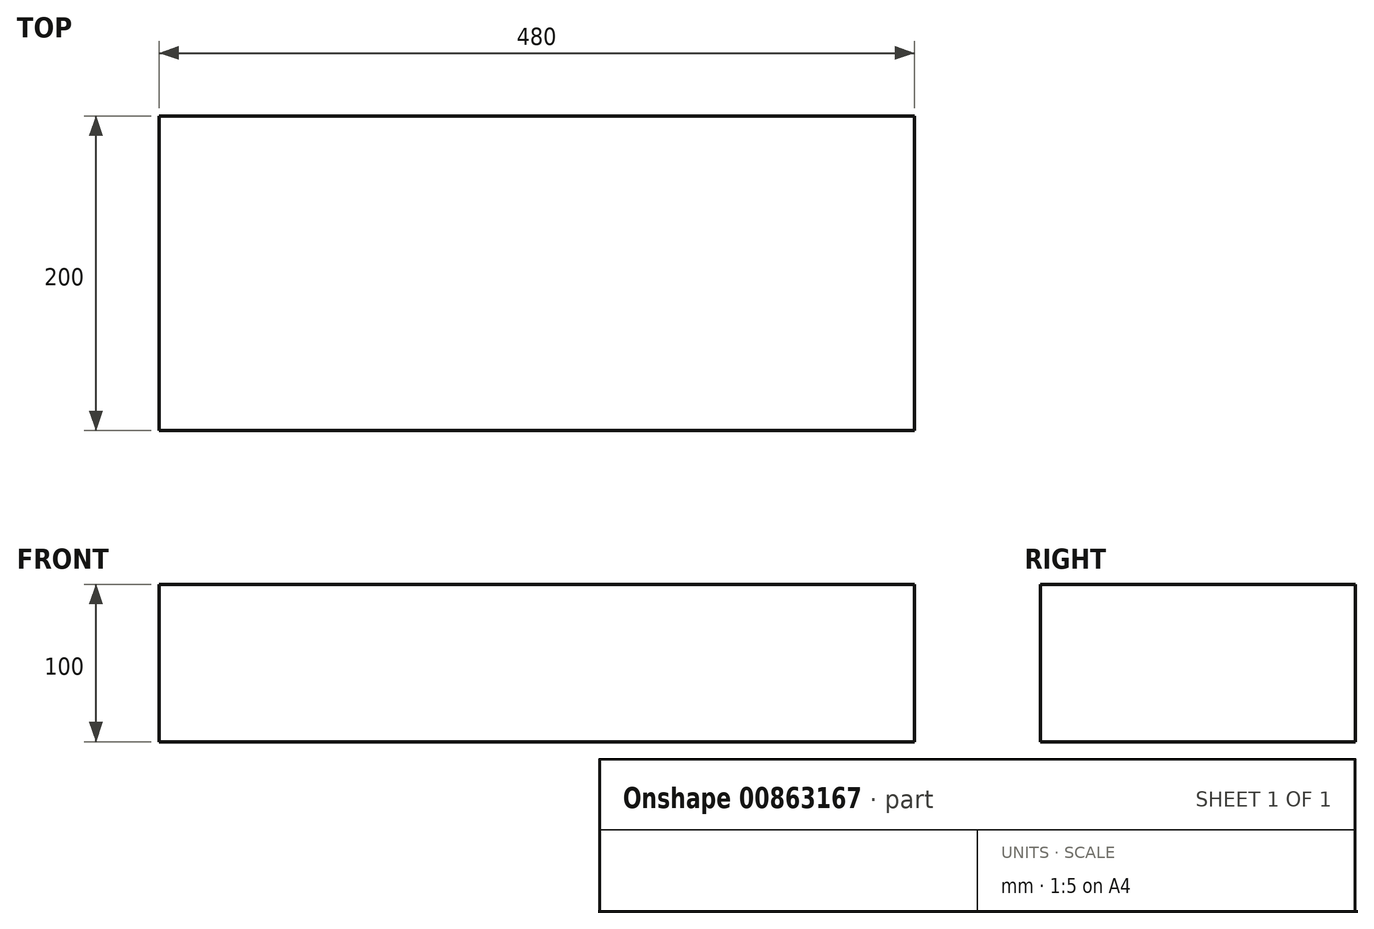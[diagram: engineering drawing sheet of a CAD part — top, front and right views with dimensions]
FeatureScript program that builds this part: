
annotation { "Feature Type Name" : "Feature", "Feature Type Description" : "" }
export const myFeature = defineFeature(function(context is Context, id is Id, definition is map)
    precondition{}
    {
        {
            var Q0;
            Q0=qCreatedBy(makeId("Top.planeOp"),FACE);
            var sketch = newSketch(context, id + "F0", { "sketchPlane" : qUnion([Q0])});
            skLineSegment(sketch, "E0", {"start": v(0, 0) * mm, "end": v(0, 200) * mm});
            skLineSegment(sketch, "E1", {"start": v(0, 200) * mm, "end": v(480, 200) * mm});
            skLineSegment(sketch, "E2", {"start": v(480, 200) * mm, "end": v(480, 0) * mm});
            skLineSegment(sketch, "E3", {"start": v(480, 0) * mm, "end": v(0, 0) * mm});
            skSolve(sketch);
        }
        {
            var Q0;
            Q0=makeQuery(id+"F0.imprint","IMPRINT",FACE,{"disambiguationData":[TD([[makeQuery(id+"F0.imprint","IMPRINT",EDGE,{"derivedFrom":sQuery(id+"F0.wireOp",EDGE,"E0")}),-1.0]])]});
            extrude(context, id + "F1", {"entities" : qUnion([Q0]), "depth" : 100 * mm, "offsetDistance" : 25 * mm});
        }
    });
